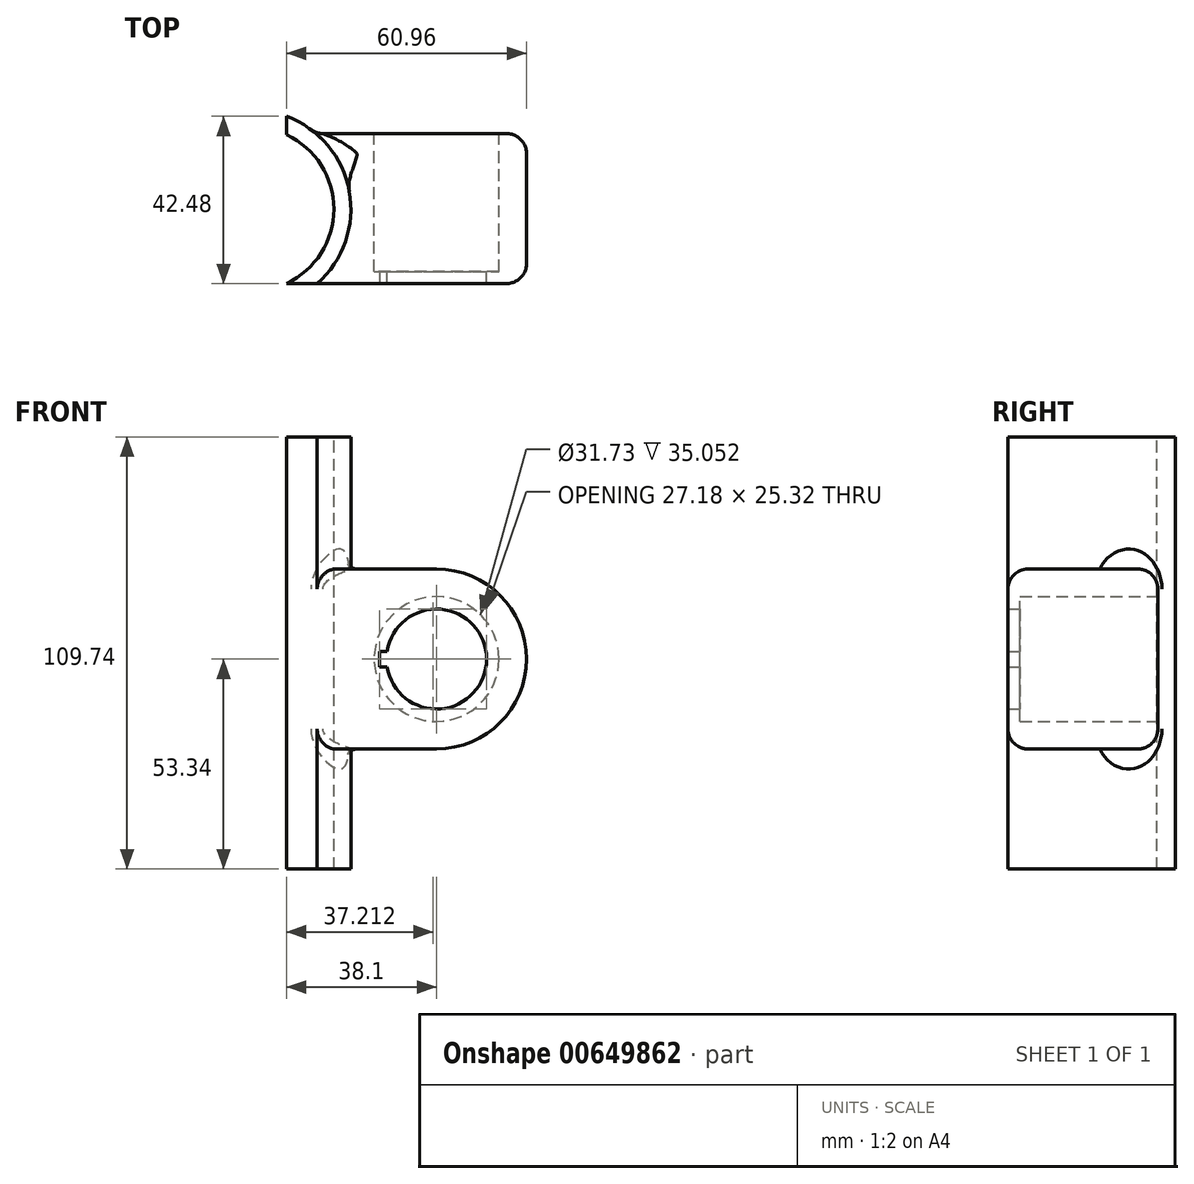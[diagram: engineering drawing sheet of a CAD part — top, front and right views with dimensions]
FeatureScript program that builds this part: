
annotation { "Feature Type Name" : "Feature", "Feature Type Description" : "" }
export const myFeature = defineFeature(function(context is Context, id is Id, definition is map)
    precondition{}
    {
        {
            var Q0;
            Q0=qCreatedBy(makeId("Front.planeOp"),FACE);
            var sketch = newSketch(context, id + "F0", { "sketchPlane" : qUnion([Q0])});
            skCircle(sketch, "E0", {"center": v(0, 0) * mm, "radius": 12.7 * mm});
            skCircle(sketch, "E1.0", {"center": v(0, 0) * mm, "radius": 22.86 * mm});
            skLineSegment(sketch, "E2", {"start": v(0, 22.86) * mm, "end": v(-38.1, 22.86) * mm});
            skLineSegment(sketch, "E3", {"start": v(0, -22.86) * mm, "end": v(-38.1, -22.86) * mm});
            skLineSegment(sketch, "E4", {"start": v(-38.1, -22.86) * mm, "end": v(-38.1, 22.86) * mm});
            skCircle(sketch, "E5", {"center": v(0, 0) * mm, "radius": 15.86 * mm});
            skSolve(sketch);
        }
        {
            var Q0;
            Q0=makeQuery(id+"F0.imprint","IMPRINT",FACE,{"disambiguationData":[TD([[makeQuery(id+"F0.imprint","IMPRINT",EDGE,{"derivedFrom":sQuery(id+"F0.wireOp",EDGE,"E0")}),-1.0]])]});
            extrude(context, id + "F1", {"entities" : qUnion([Q0]), "depth" : 38.1 * mm, "offsetDistance" : 25.4 * mm});
        }
        {
            var Q0;
            Q0=qCreatedBy(makeId("Front.planeOp"),FACE);
            var sketch = newSketch(context, id + "F2", { "sketchPlane" : qUnion([Q0])});
            skCircle(sketch, "E6.0", {"center": v(0, 0) * mm, "radius": 16.51 * mm});
            skSolve(sketch);
        }
        {
            var Q0;
            Q0=makeQuery(id+"F2.imprint","IMPRINT",FACE,{"disambiguationData":[TD([[makeQuery(id+"F2.imprint","IMPRINT",EDGE,{"derivedFrom":sQuery(id+"F2.wireOp",EDGE,"E6.0")}),1.0]])]});
            extrude(context, id + "F3", {"entities" : qUnion([Q0]), "operationType" : NewBodyOperationType.REMOVE, "depth" : 35.05 * mm, "offsetDistance" : 25.4 * mm});
        }
        {
            var Q0;
            Q0 = qSketchRegion(id + "F0", true);
            extrude(context, id + "F4", {"entities" : qUnion([Q0]), "operationType" : NewBodyOperationType.ADD, "depth" : 38.1 * mm, "offsetDistance" : 25.4 * mm});
        }
        {
            var Q0;
            Q0=makeQuery(id+"F4.opExtrude","SWEPT_FACE",FACE,{"disambiguationData":[OSD([sQuery(id+"F0.wireOp",EDGE,"E2")])]});
            var sketch = newSketch(context, id + "F5", { "sketchPlane" : qUnion([Q0])});
            skArc(sketch, "E7", {"start": v(-38.1, -38.05) * mm, "mid": v(-26.07, -19.18) * mm, "end": v(-38.1, -0.3) * mm});
            skArc(sketch, "E8.0", {"start": v(-38.1, -42.73) * mm, "mid": v(-21.76, -19.18) * mm, "end": v(-38.1, 4.38) * mm});
            skLineSegment(sketch, "E9", {"start": v(-38.1, -38.05) * mm, "end": v(-38.1, -42.73) * mm});
            skLineSegment(sketch, "E10", {"start": v(-38.1, -0.3) * mm, "end": v(-38.1, 4.38) * mm});
            skPoint(sketch, "E11.orphan", {"position": v(-38.1, -19.05) * mm});
            skPoint(sketch, "E12.start.orphan", {"position": v(-87.75, -67.46) * mm});
            skPoint(sketch, "E13.orphan", {"position": v(-38.1, -67.46) * mm});
            skSolve(sketch);
        }
        {
            var Q0;
            Q0 = qSketchRegion(id + "F5", true);
            extrude(context, id + "F6", {"entities" : qUnion([Q0]), "operationType" : NewBodyOperationType.ADD, "oppositeDirection" : true, "depth" : 76.2 * mm, "offsetDistance" : 25.4 * mm});
        }
        {
            var Q0;
            Q0 = qSketchRegion(id + "F5", true);
            extrude(context, id + "F7", {"entities" : qUnion([Q0]), "operationType" : NewBodyOperationType.ADD, "oppositeDirection" : true, "depth" : 70.36 * mm, "offsetDistance" : 25.4 * mm, "hasSecondDirection" : true, "secondDirectionOppositeDirection" : false, "secondDirectionDepth" : 23.62 * mm});
        }
        {
            var Q0;
            {var subQ0=sQuery(id+"F5.wireOp",EDGE,"E9");var subQ1=sQuery(id+"F5.wireOp",EDGE,"E8.0");var subQ2=makeQuery(id+"F5.imprint","INTERSECT",VERTEX,{"derivedFrom":[subQ1,subQ0]});Q0=makeQuery(id+"F5.imprint","IMPRINT",FACE,{"disambiguationData":[TD([[makeQuery(id+"F5.imprint","IMPRINT",EDGE,{"disambiguationData":[TD([[subQ2,-1.0]])],"derivedFrom":subQ1}),1.0]])]});}
            var Q1;
            {var subQ4=sQuery(id+"F5.wireOp",EDGE,"E7");Q1=makeQuery(id+"F5.imprint","IMPRINT",FACE,{"disambiguationData":[TD([[makeQuery(id+"F5.imprint","IMPRINT",EDGE,{"derivedFrom":subQ4}),-1.0]])]});}
            var Q2;
            {var subQ0=sQuery(id+"F5.wireOp",EDGE,"E10");var subQ1=sQuery(id+"F5.wireOp",EDGE,"E8.0");var subQ2=makeQuery(id+"F5.imprint","INTERSECT",VERTEX,{"derivedFrom":[subQ1,subQ0]});Q2=makeQuery(id+"F5.imprint","IMPRINT",FACE,{"disambiguationData":[TD([[makeQuery(id+"F5.imprint","IMPRINT",EDGE,{"disambiguationData":[TD([[subQ2,1.0]])],"derivedFrom":subQ1}),1.0]])]});}
            extrude(context, id + "F8", {"entities" : qUnion([Q0, Q1, Q2]), "operationType" : NewBodyOperationType.ADD, "depth" : 33.54 * mm, "offsetDistance" : 25.4 * mm});
        }
        {
            var Q0;
            {var subQ0=sQuery(id+"F5.wireOp",EDGE,"E7");Q0=makeQuery(id+"F5.imprint","IMPRINT",FACE,{"disambiguationData":[TD([[makeQuery(id+"F5.imprint","IMPRINT",EDGE,{"derivedFrom":subQ0}),1.0]])]});}
            extrude(context, id + "F9", {"entities" : qUnion([Q0]), "operationType" : NewBodyOperationType.REMOVE, "oppositeDirection" : true, "depth" : 108.46 * mm, "offsetDistance" : 25.4 * mm});
        }
        {
            var Q0;
            {var subQ0=sQuery(id+"F0.wireOp",EDGE,"E5");Q0=makeQuery(id+"F4.boolean.opBoolean","MERGE",FACE,{"derivedFrom":[makeQuery(id+"F1.opExtrude","CAP_FACE",FACE,{"disambiguationData":[OSD([sQuery(id+"F0.wireOp",EDGE,"E0"),subQ0])],"isStart":false}),makeQuery(id+"F4.opExtrude","CAP_FACE",FACE,{"disambiguationData":[OSD([sQuery(id+"F0.wireOp",EDGE,"E1.0"),sQuery(id+"F0.wireOp",EDGE,"E2"),sQuery(id+"F0.wireOp",EDGE,"E3"),sQuery(id+"F0.wireOp",EDGE,"E4"),subQ0])],"isStart":false})]});}
            var sketch = newSketch(context, id + "F10", { "sketchPlane" : qUnion([Q0])});
            skLineSegment(sketch, "E14.bottom", {"start": v(-19.3, 8.15) * mm, "end": v(-75.16, 8.15) * mm});
            skLineSegment(sketch, "E14.top", {"start": v(-19.3, -89.88) * mm, "end": v(-75.16, -89.88) * mm});
            skLineSegment(sketch, "E14.left", {"start": v(-19.3, 8.15) * mm, "end": v(-19.3, -89.88) * mm});
            skLineSegment(sketch, "E14.right", {"start": v(-75.16, 8.15) * mm, "end": v(-75.16, -89.88) * mm});
            skLineSegment(sketch, "E15.bottom", {"start": v(-19.3, -4) * mm, "end": v(-86.87, -4) * mm});
            skLineSegment(sketch, "E15.top", {"start": v(-19.3, 90.17) * mm, "end": v(-86.87, 90.17) * mm});
            skLineSegment(sketch, "E15.left", {"start": v(-19.3, -4) * mm, "end": v(-19.3, 90.17) * mm});
            skLineSegment(sketch, "E15.right", {"start": v(-86.87, -4) * mm, "end": v(-86.87, 90.17) * mm});
            skSolve(sketch);
        }
        {
            var Q0;
            Q0 = qSketchRegion(id + "F10", true);
            extrude(context, id + "F11", {"entities" : qUnion([Q0]), "operationType" : NewBodyOperationType.REMOVE, "depth" : 25.4 * mm, "offsetDistance" : 25.4 * mm});
        }
        {
            var Q0;
            Q0=makeQuery(id+"F8.opExtrude","CAP_EDGE",EDGE,{"disambiguationData":[OSD([sQuery(id+"F5.wireOp",EDGE,"E8.0")])],"isStart":true});
            var Q1;
            Q1=makeQuery(id+"F6.boolean.opBoolean","INTERSECT",EDGE,{"derivedFrom":[makeQuery(id+"F4.opExtrude","CAP_FACE",FACE,{"disambiguationData":[OSD([sQuery(id+"F0.wireOp",EDGE,"E1.0"),sQuery(id+"F0.wireOp",EDGE,"E2"),sQuery(id+"F0.wireOp",EDGE,"E3"),sQuery(id+"F0.wireOp",EDGE,"E4"),sQuery(id+"F0.wireOp",EDGE,"E5")])],"isStart":true}),makeQuery(id+"F6.opExtrude","SWEPT_FACE",FACE,{"disambiguationData":[OSD([sQuery(id+"F5.wireOp",EDGE,"E8.0")])]})]});
            var Q2;
            Q2=makeQuery(id+"F4.opExtrude","CAP_EDGE",EDGE,{"disambiguationData":[OSD([sQuery(id+"F0.wireOp",EDGE,"E2")])],"isStart":true});
            var Q3;
            Q3=makeQuery(id+"F4.opExtrude","CAP_EDGE",EDGE,{"disambiguationData":[OSD([sQuery(id+"F0.wireOp",EDGE,"E1.0")])],"isStart":false});
            fillet(context, id + "F12", {"entities" : qUnion([Q0, Q1, Q2, Q3]), "radius" : 5.08 * mm, "tangentPropagation" : true, "allowEdgeOverflow" : false});
        }
        {
            var Q0;
            {var subQ0=sQuery(id+"F0.wireOp",EDGE,"E5");Q0=makeQuery(id+"F11.boolean.opBoolean","MERGE",FACE,{"derivedFrom":[makeQuery(id+"F4.boolean.opBoolean","MERGE",FACE,{"derivedFrom":[makeQuery(id+"F1.opExtrude","CAP_FACE",FACE,{"disambiguationData":[OSD([sQuery(id+"F0.wireOp",EDGE,"E0"),subQ0])],"isStart":false}),makeQuery(id+"F4.opExtrude","CAP_FACE",FACE,{"disambiguationData":[OSD([sQuery(id+"F0.wireOp",EDGE,"E1.0"),sQuery(id+"F0.wireOp",EDGE,"E2"),sQuery(id+"F0.wireOp",EDGE,"E3"),sQuery(id+"F0.wireOp",EDGE,"E4"),subQ0])],"isStart":false})]}),makeQuery(id+"F11.opExtrude","CAP_FACE",FACE,{"disambiguationData":[OSD([sQuery(id+"F10.wireOp",EDGE,"E14.top"),sQuery(id+"F10.wireOp",EDGE,"E14.left"),sQuery(id+"F10.wireOp",EDGE,"E14.right"),sQuery(id+"F10.wireOp",EDGE,"E15.bottom"),sQuery(id+"F10.wireOp",EDGE,"E15.top"),sQuery(id+"F10.wireOp",EDGE,"E15.left"),sQuery(id+"F10.wireOp",EDGE,"E15.right")])],"isStart":true})]});}
            var sketch = newSketch(context, id + "F13", { "sketchPlane" : qUnion([Q0])});
            skLineSegment(sketch, "E16.bottom", {"start": v(-14.48, -1.97) * mm, "end": v(-4.21, -1.97) * mm});
            skLineSegment(sketch, "E16.top", {"start": v(-14.48, 1.97) * mm, "end": v(-4.21, 1.97) * mm});
            skLineSegment(sketch, "E16.left", {"start": v(-14.48, -1.97) * mm, "end": v(-14.48, 1.97) * mm});
            skPoint(sketch, "E16.middle", {"position": v(0, 0) * mm});
            skLineSegment(sketch, "E17", {"start": v(-4.21, 1.97) * mm, "end": v(-4.21, -1.97) * mm});
            skPoint(sketch, "E16.right.start.orphan", {"position": v(14.48, -1.97) * mm});
            skPoint(sketch, "E18.orphan", {"position": v(14.48, 1.97) * mm});
            skSolve(sketch);
        }
        {
            var Q0;
            Q0 = qSketchRegion(id + "F13", true);
            extrude(context, id + "F14", {"entities" : qUnion([Q0]), "operationType" : NewBodyOperationType.REMOVE, "endBound" : BoundingType.THROUGH_ALL, "oppositeDirection" : true, "depth" : 25.4 * mm, "offsetDistance" : 25.4 * mm});
        }
    });
